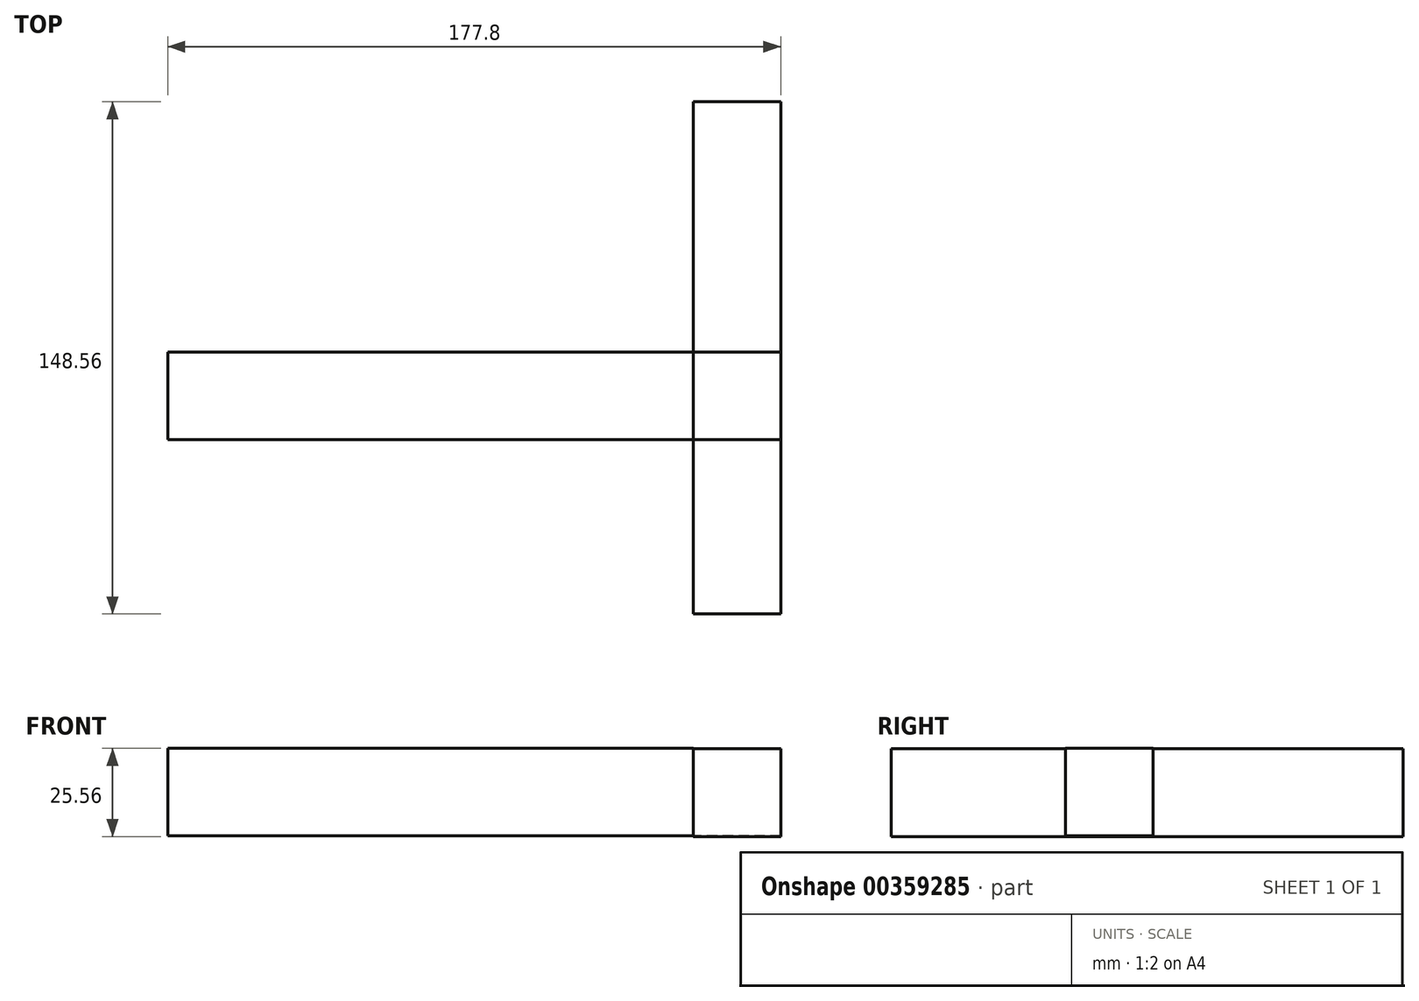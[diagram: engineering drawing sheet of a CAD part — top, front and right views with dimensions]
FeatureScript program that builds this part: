
annotation { "Feature Type Name" : "Feature", "Feature Type Description" : "" }
export const myFeature = defineFeature(function(context is Context, id is Id, definition is map)
    precondition{}
    {
        {
            var Q0;
            Q0=qCreatedBy(makeId("Top.planeOp"),FACE);
            var sketch = newSketch(context, id + "F0", { "sketchPlane" : qUnion([Q0])});
            skLineSegment(sketch, "E0.bottom", {"start": v(0, 0) * mm, "end": v(152.4, 0) * mm});
            skLineSegment(sketch, "E0.top", {"start": v(0, -25.4) * mm, "end": v(152.4, -25.4) * mm});
            skLineSegment(sketch, "E0.left", {"start": v(0, 0) * mm, "end": v(0, -25.4) * mm});
            skLineSegment(sketch, "E0.right", {"start": v(152.4, 0) * mm, "end": v(152.4, -25.4) * mm});
            skSolve(sketch);
        }
        {
            var Q0;
            Q0 = qSketchRegion(id + "F0", true);
            extrude(context, id + "F1", {"entities" : qUnion([Q0]), "depth" : 25.4 * mm});
        }
        {
            var Q0;
            Q0=makeQuery(id+"F1.opExtrude","SWEPT_FACE",FACE,{"disambiguationData":[OSD([sQuery(id+"F0.wireOp",EDGE,"E0.right")])]});
            var sketch = newSketch(context, id + "F2", { "sketchPlane" : qUnion([Q0])});
            skCircle(sketch, "E1", {"center": v(-12.55, 12.7) * mm, "radius": 7.62 * mm});
            skPoint(sketch, "E1.centerSnap0", {"position": v(0, 12.7) * mm});
            skSolve(sketch);
        }
        {
            var Q0;
            Q0=makeQuery(id+"F2.imprint","IMPRINT",FACE,{"disambiguationData":[TD([[makeQuery(id+"F2.imprint","IMPRINT",EDGE,{"derivedFrom":sQuery(id+"F2.wireOp",EDGE,"E1")}),-1.0]])]});
            var sketch = newSketch(context, id + "F3", { "sketchPlane" : qUnion([Q0])});
            skLineSegment(sketch, "E2.bottom", {"start": v(72.53, -0.16) * mm, "end": v(-76.03, -0.16) * mm});
            skLineSegment(sketch, "E2.top", {"start": v(72.53, 25.3) * mm, "end": v(-76.03, 25.3) * mm});
            skLineSegment(sketch, "E2.left", {"start": v(72.53, -0.16) * mm, "end": v(72.53, 25.3) * mm});
            skLineSegment(sketch, "E2.right", {"start": v(-76.03, -0.16) * mm, "end": v(-76.03, 25.3) * mm});
            skSolve(sketch);
        }
        {
            var Q0;
            Q0=makeQuery(id+"F3.imprint","IMPRINT",FACE,{"disambiguationData":[TD([[makeQuery(id+"F3.imprint","IMPRINT",EDGE,{"derivedFrom":sQuery(id+"F3.wireOp",EDGE,"E2.bottom")}),-1.0]])]});
            extrude(context, id + "F4", {"entities" : qUnion([Q0]), "depth" : 25.4 * mm});
        }
    });
